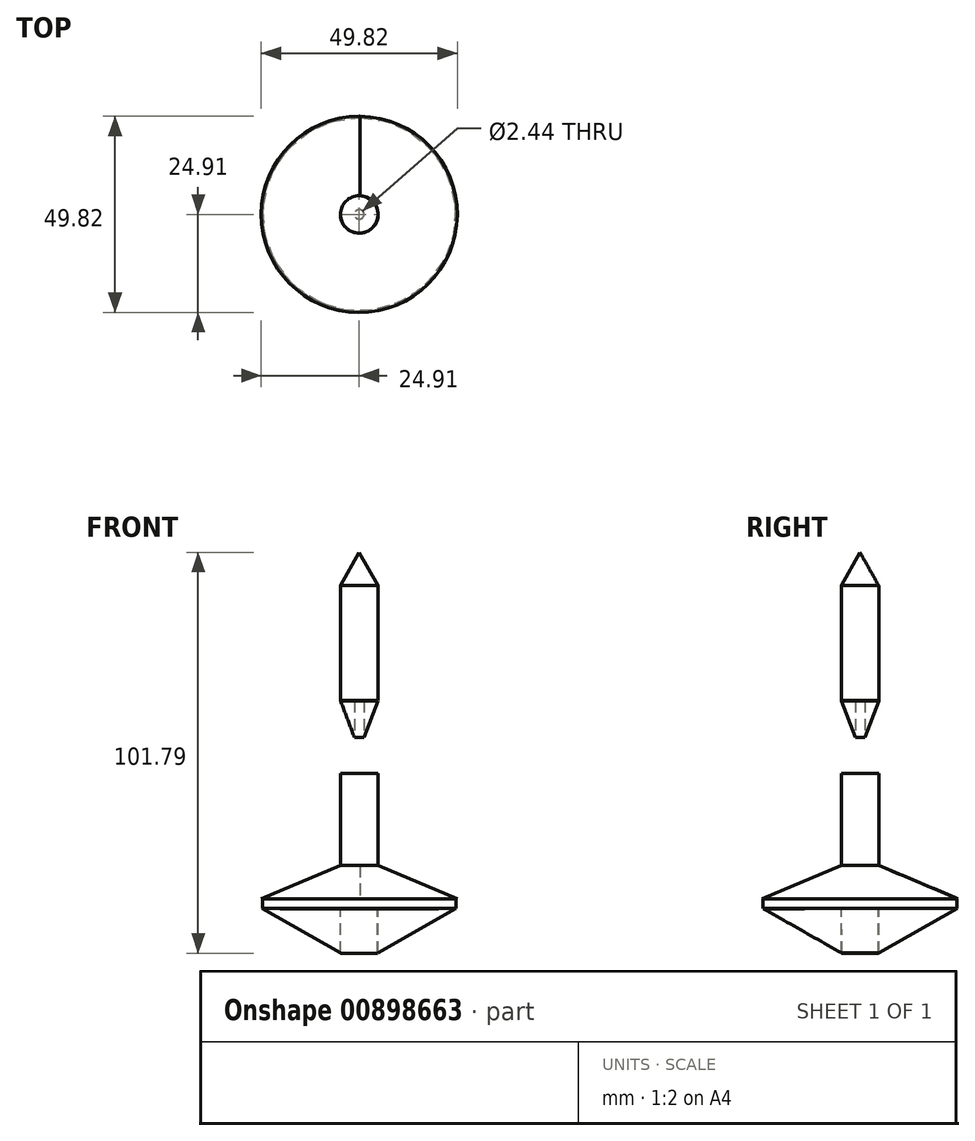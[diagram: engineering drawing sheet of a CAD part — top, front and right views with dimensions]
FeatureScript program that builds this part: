
annotation { "Feature Type Name" : "Feature", "Feature Type Description" : "" }
export const myFeature = defineFeature(function(context is Context, id is Id, definition is map)
    precondition{}
    {
        {
            var Q0;
            Q0=qCreatedBy(makeId("Top.planeOp"),FACE);
            var sketch = newSketch(context, id + "F0", { "sketchPlane" : qUnion([Q0])});
            skCircle(sketch, "E0", {"center": v(0, 0) * mm, "radius": 24.62 * mm});
            skCircle(sketch, "E1", {"center": v(0, 0) * mm, "radius": 4.78 * mm});
            skSolve(sketch);
        }
        {
            var Q0;
            Q0=makeQuery(id+"F0.imprint","IMPRINT",FACE,{"disambiguationData":[TD([[makeQuery(id+"F0.imprint","IMPRINT",EDGE,{"derivedFrom":sQuery(id+"F0.wireOp",EDGE,"E0")}),1.0]])]});
            extrude(context, id + "F1", {"entities" : qUnion([Q0]), "depth" : 2.54 * mm, "offsetDistance" : 25.4 * mm});
        }
        {
            var Q0;
            Q0=makeQuery(id+"F0.imprint","IMPRINT",FACE,{"disambiguationData":[TD([[makeQuery(id+"F0.imprint","IMPRINT",EDGE,{"derivedFrom":sQuery(id+"F0.wireOp",EDGE,"E1")}),1.0]])]});
            extrude(context, id + "F2", {"entities" : qUnion([Q0]), "operationType" : NewBodyOperationType.ADD, "depth" : 34.3 * mm, "offsetDistance" : 25.4 * mm});
        }
        {
            var Q0;
            Q0=qCreatedBy(makeId("Right.planeOp"),FACE);
            var sketch = newSketch(context, id + "F3", { "sketchPlane" : qUnion([Q0])});
            skLineSegment(sketch, "E2", {"start": v(24.91, 2.5) * mm, "end": v(4.75, 10.95) * mm});
            skLineSegment(sketch, "E3", {"start": v(24.91, 2.5) * mm, "end": v(4.74, 2.52) * mm});
            skLineSegment(sketch, "E4", {"start": v(4.74, 2.52) * mm, "end": v(4.75, 10.95) * mm});
            skLineSegment(sketch, "E5", {"start": v(0, 90.46) * mm, "end": v(-4.76, 82.03) * mm});
            skLineSegment(sketch, "E6", {"start": v(-4.76, 82.03) * mm, "end": v(0, 82.03) * mm});
            skPoint(sketch, "E7", {"position": v(0, 82.03) * mm});
            skLineSegment(sketch, "E8", {"start": v(0, 82.03) * mm, "end": v(0, 70.97) * mm});
            skLineSegment(sketch, "E9", {"start": v(0, 90.46) * mm, "end": v(0, 82.03) * mm});
            skPoint(sketch, "E10.orphan", {"position": v(4.76, 82.03) * mm});
            skLineSegment(sketch, "E11", {"start": v(4.76, 0) * mm, "end": v(4.75, -11.32) * mm});
            skLineSegment(sketch, "E12", {"start": v(4.75, -11.32) * mm, "end": v(24.67, 0) * mm});
            skLineSegment(sketch, "E13", {"start": v(24.67, 0) * mm, "end": v(4.76, 0) * mm});
            skPoint(sketch, "E14", {"position": v(0, 0) * mm});
            skSolve(sketch);
        }
        {
            var Q0;
            Q0=makeQuery(id+"F3.imprint","IMPRINT",FACE,{"disambiguationData":[TD([[makeQuery(id+"F3.imprint","IMPRINT",EDGE,{"derivedFrom":sQuery(id+"F3.wireOp",EDGE,"E2")}),1.0]])]});
            extrude(context, id + "F4", {"entities" : qUnion([Q0]), "operationType" : NewBodyOperationType.ADD, "depth" : 0.25 * mm, "offsetDistance" : 25.4 * mm});
        }
        {
            var Q0;
            Q0=makeQuery(id+"F4.opExtrude","CAP_FACE",FACE,{"disambiguationData":[OSD([sQuery(id+"F3.wireOp",EDGE,"E2"),sQuery(id+"F3.wireOp",EDGE,"E3"),sQuery(id+"F3.wireOp",EDGE,"E4")])],"isStart":true});
            var Q1;
            Q1=sQuery(id+"F0.wireOp",EDGE,"E1");
            revolve(context, id + "F5", {"operationType" : NewBodyOperationType.ADD, "surfaceOperationType" : NewSurfaceOperationType.NEW, "entities" : qUnion([Q0]), "axis" : qUnion([Q1]), "revolveType" : RevolveType.FULL});
        }
        {
            var Q0;
            Q0=makeQuery(id+"F2.opExtrude","CAP_FACE",FACE,{"disambiguationData":[OSD([sQuery(id+"F0.wireOp",EDGE,"E1")])],"isStart":false});
            var sketch = newSketch(context, id + "F6", { "sketchPlane" : qUnion([Q0])});
            skCircle(sketch, "E15", {"center": v(0, 0) * mm, "radius": 1.25 * mm});
            skSolve(sketch);
        }
        {
            var Q0;
            Q0=makeQuery(id+"F3.imprint","IMPRINT",FACE,{"disambiguationData":[TD([[makeQuery(id+"F3.imprint","IMPRINT",EDGE,{"derivedFrom":sQuery(id+"F3.wireOp",EDGE,"E11")}),1.0]])]});
            var Q1;
            Q1=sQuery(id+"F3.wireOp",EDGE,"E8");
            revolve(context, id + "F7", {"operationType" : NewBodyOperationType.ADD, "surfaceOperationType" : NewSurfaceOperationType.NEW, "entities" : qUnion([Q0]), "axis" : qUnion([Q1]), "revolveType" : RevolveType.FULL});
        }
        {
            var Q0;
            Q0=qCreatedBy(makeId("Top.planeOp"),FACE);
            var sketch = newSketch(context, id + "F8", { "sketchPlane" : qUnion([Q0])});
            skCircle(sketch, "E16", {"center": v(0, 0) * mm, "radius": 4.7 * mm});
            skSolve(sketch);
        }
        {
            var Q0;
            Q0=makeQuery(id+"F8.imprint","IMPRINT",FACE,{"disambiguationData":[TD([[makeQuery(id+"F8.imprint","IMPRINT",EDGE,{"derivedFrom":sQuery(id+"F8.wireOp",EDGE,"E16")}),1.0]])]});
            extrude(context, id + "F9", {"entities" : qUnion([Q0]), "oppositeDirection" : true, "depth" : 11.33 * mm, "offsetDistance" : 25.4 * mm});
        }
        {
            var Q0;
            Q0=makeQuery(id+"F3.imprint","IMPRINT",FACE,{"disambiguationData":[TD([[makeQuery(id+"F3.imprint","IMPRINT",EDGE,{"derivedFrom":sQuery(id+"F3.wireOp",EDGE,"E5")}),1.0]])]});
            var Q1;
            Q1=sQuery(id+"F3.wireOp",EDGE,"E9");
            revolve(context, id + "F10", {"operationType" : NewBodyOperationType.ADD, "surfaceOperationType" : NewSurfaceOperationType.NEW, "entities" : qUnion([Q0]), "axis" : qUnion([Q1]), "revolveType" : RevolveType.FULL});
        }
        {
            var Q0;
            Q0=qCreatedBy(makeId("Front.planeOp"),FACE);
            var sketch = newSketch(context, id + "F11", { "sketchPlane" : qUnion([Q0])});
            skLineSegment(sketch, "E17", {"start": v(-1.22, 34.3) * mm, "end": v(-1.22, 43.67) * mm});
            skLineSegment(sketch, "E18", {"start": v(-1.22, 43.67) * mm, "end": v(-4.77, 34.3) * mm});
            skLineSegment(sketch, "E19", {"start": v(-4.77, 34.3) * mm, "end": v(-1.22, 34.3) * mm});
            skLineSegment(sketch, "E20", {"start": v(-1.26, 43.56) * mm, "end": v(-1.22, 43.56) * mm});
            skLineSegment(sketch, "E21.MirrorCS", {"start": v(-1.22, 43.45) * mm, "end": v(-4.77, 52.82) * mm});
            skLineSegment(sketch, "E22.MirrorCS", {"start": v(-1.22, 52.82) * mm, "end": v(-1.22, 43.45) * mm});
            skLineSegment(sketch, "E23.MirrorCS", {"start": v(-4.77, 52.82) * mm, "end": v(-1.22, 52.82) * mm});
            skSolve(sketch);
        }
        {
            var Q0;
            Q0=makeQuery(id+"F6.imprint","IMPRINT",FACE,{"disambiguationData":[TD([[makeQuery(id+"F6.imprint","IMPRINT",EDGE,{"derivedFrom":sQuery(id+"F6.wireOp",EDGE,"E15")}),-1.0]])]});
            var sketch = newSketch(context, id + "F12", { "sketchPlane" : qUnion([Q0])});
            skCircle(sketch, "E24", {"center": v(0, 0) * mm, "radius": 2.81 * mm});
            skSolve(sketch);
        }
        {
            var Q0;
            {var subQ0=sQuery(id+"F11.wireOp",EDGE,"E17");Q0=makeQuery(id+"F11.imprint","IMPRINT",FACE,{"disambiguationData":[TD([[makeQuery(id+"F11.imprint","IMPRINT",EDGE,{"derivedFrom":subQ0}),1.0]])]});}
            var Q1;
            {var subQ5=sQuery(id+"F11.wireOp",EDGE,"E23.MirrorCS");Q1=makeQuery(id+"F11.imprint","IMPRINT",FACE,{"disambiguationData":[TD([[makeQuery(id+"F11.imprint","IMPRINT",EDGE,{"derivedFrom":subQ5}),-1.0]])]});}
            var Q2;
            Q2=sQuery(id+"F12.wireOp",EDGE,"E24");
            revolve(context, id + "F13", {"surfaceOperationType" : NewSurfaceOperationType.NEW, "entities" : qUnion([Q0, Q1]), "axis" : qUnion([Q2]), "revolveType" : RevolveType.FULL});
        }
        {
            var Q0;
            Q0=makeQuery(id+"F10.opRevolve","SWEPT_FACE",FACE,{"disambiguationData":[OSD([sQuery(id+"F3.wireOp",EDGE,"E6")])]});
            var sketch = newSketch(context, id + "F14", { "sketchPlane" : qUnion([Q0])});
            skCircle(sketch, "E25", {"center": v(0, 0) * mm, "radius": 4.76 * mm});
            skSolve(sketch);
        }
        {
            var Q0;
            {var subQ0=sQuery(id+"F14.wireOp",EDGE,"E25");var subQ1=makeQuery(id+"F10.opRevolve","SWEPT_EDGE",EDGE,{"disambiguationData":[OSD([sQuery(id+"F3.wireOp",EDGE,"E5"),sQuery(id+"F3.wireOp",EDGE,"E6")])]});var subQ2=makeQuery(id+"F14.imprint","INTERSECT",VERTEX,{"disambiguationData":[OD(0.0)],"derivedFrom":[subQ1,subQ0]});Q0=makeQuery(id+"F14.imprint","IMPRINT",FACE,{"disambiguationData":[TD([[makeQuery(id+"F14.imprint","IMPRINT",EDGE,{"disambiguationData":[TD([[subQ2,-1.0]])],"derivedFrom":subQ0}),1.0]])]});}
            extrude(context, id + "F15", {"entities" : qUnion([Q0]), "depth" : 29.3 * mm, "offsetDistance" : 25.4 * mm});
        }
    });
